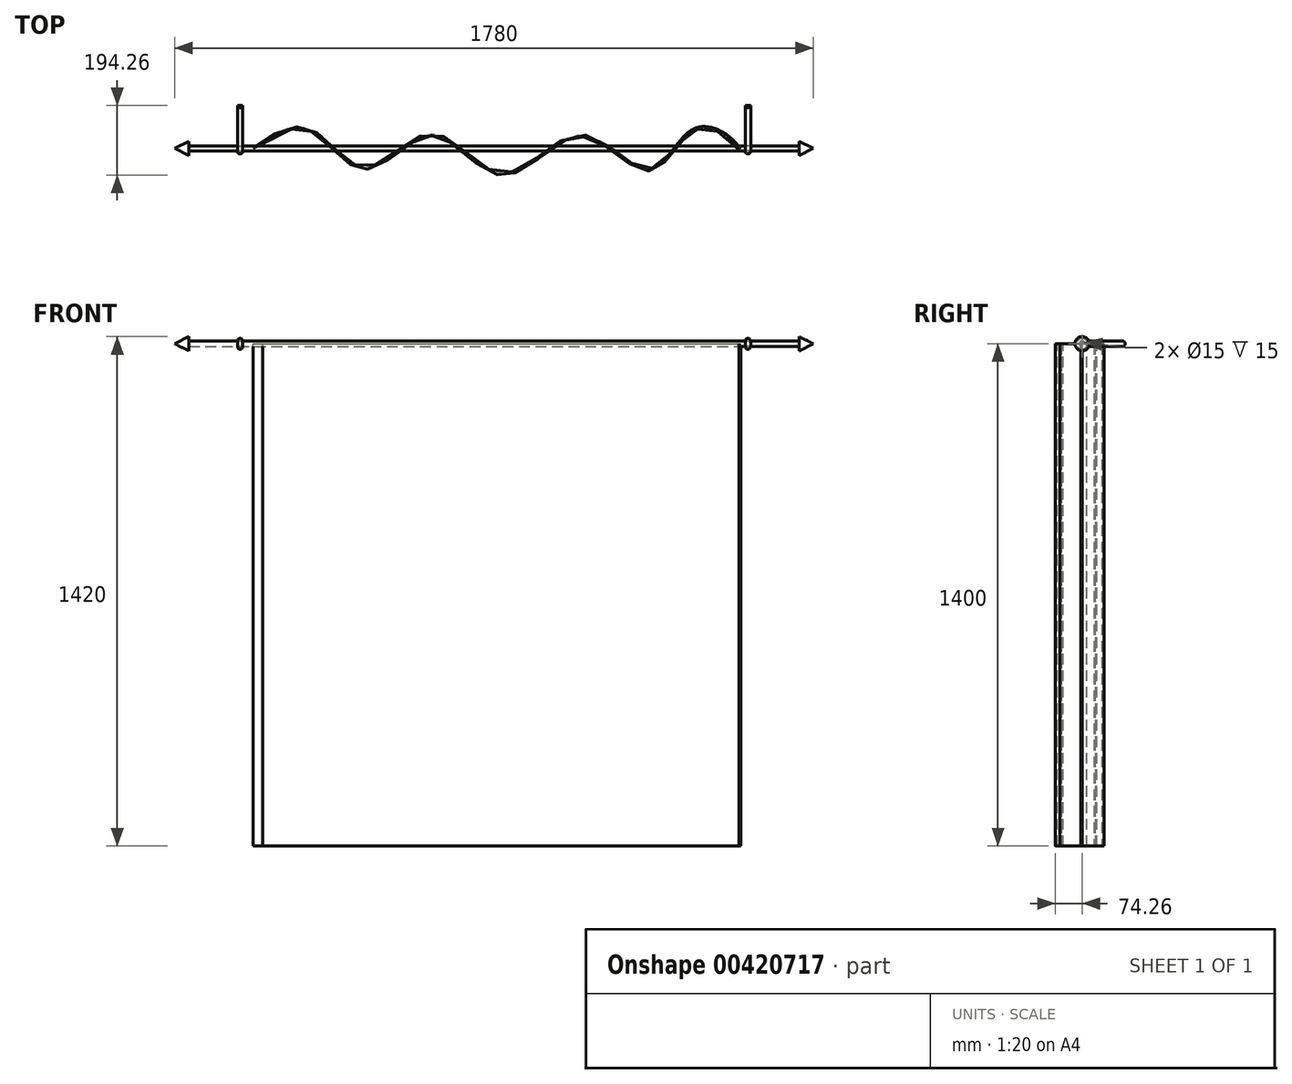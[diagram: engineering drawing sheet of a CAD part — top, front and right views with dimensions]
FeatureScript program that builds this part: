
annotation { "Feature Type Name" : "Feature", "Feature Type Description" : "" }
export const myFeature = defineFeature(function(context is Context, id is Id, definition is map)
    precondition{}
    {
        {
            var Q0;
            Q0=qCreatedBy(makeId("Front.planeOp"),FACE);
            var sketch = newSketch(context, id + "F0", { "sketchPlane" : qUnion([Q0])});
            skLineSegment(sketch, "E0", {"start": v(-890, 0) * mm, "end": v(-850, 20) * mm});
            skLineSegment(sketch, "E1", {"start": v(-850, 20) * mm, "end": v(-850, 7.5) * mm});
            skLineSegment(sketch, "E2", {"start": v(-850, 7.5) * mm, "end": v(850, 7.5) * mm});
            skLineSegment(sketch, "E3", {"start": v(850, 7.5) * mm, "end": v(850, 20) * mm});
            skLineSegment(sketch, "E4", {"start": v(850, 20) * mm, "end": v(890, 0) * mm});
            skLineSegment(sketch, "E5", {"start": v(890, 0) * mm, "end": v(-890, 0) * mm});
            skSolve(sketch);
        }
        {
            var Q0;
            Q0 = qSketchRegion(id + "F0", true);
            var Q1;
            Q1=sQuery(id+"F0.wireOp",EDGE,"E5");
            revolve(context, id + "F1", {"entities" : qUnion([Q0]), "axis" : qUnion([Q1]), "revolveType" : RevolveType.FULL});
        }
        {
            var Q0;
            Q0=qCreatedBy(makeId("Right.planeOp"),FACE);
            cPlane(context, id + "F2", {"entities" : qUnion([Q0]), "cplaneType" : CPlaneType.OFFSET, "offset" : 700 * mm, "width" : 150 * mm, "height" : 150 * mm});
        }
        {
            var Q0;
            Q0=qCreatedBy(id+"F2.planeOp",FACE);
            var sketch = newSketch(context, id + "F3", { "sketchPlane" : qUnion([Q0])});
            skLineSegment(sketch, "E6.bottom", {"start": v(13, 7.5) * mm, "end": v(120, 7.5) * mm});
            skLineSegment(sketch, "E6.top", {"start": v(13, -7.5) * mm, "end": v(120, -7.5) * mm});
            skLineSegment(sketch, "E6.right", {"start": v(120, 7.5) * mm, "end": v(120, -7.5) * mm});
            skArc(sketch, "E7", {"start": v(13, 7.5) * mm, "mid": v(-15, 0) * mm, "end": v(13, -7.5) * mm});
            skCircle(sketch, "E8", {"center": v(0, 0) * mm, "radius": 7.5 * mm});
            skSolve(sketch);
        }
        {
            var Q0;
            Q0 = qSketchRegion(id + "F3", true);
            extrude(context, id + "F4", {"entities" : qUnion([Q0]), "depth" : 15 * mm});
        }
        {
            var Q0;
            Q0=makeQuery(id+"F4.opExtrude","SWEPT_FACE",FACE,{"disambiguationData":[OSD([sQuery(id+"F3.wireOp",EDGE,"E6.bottom")])]});
            var Q1;
            Q1=makeQuery(id+"F4.opExtrude","SWEPT_FACE",FACE,{"disambiguationData":[OSD([sQuery(id+"F3.wireOp",EDGE,"E7")])]});
            var Q2;
            Q2=makeQuery(id+"F4.opExtrude","SWEPT_FACE",FACE,{"disambiguationData":[OSD([sQuery(id+"F3.wireOp",EDGE,"E6.top")])]});
            fillet(context, id + "F5", {"entities" : qUnion([Q0, Q1, Q2]), "radius" : 7 * mm, "tangentPropagation" : true, "allowEdgeOverflow" : false});
        }
        {
            var Q0;
            Q0=makeQuery(id+"F4.opExtrude","SWEPT_BODY",BODY,{"disambiguationData":[OSD([sQuery(id+"F3.wireOp",EDGE,"E6.bottom"),sQuery(id+"F3.wireOp",EDGE,"E6.top"),sQuery(id+"F3.wireOp",EDGE,"E6.right"),sQuery(id+"F3.wireOp",EDGE,"E7"),sQuery(id+"F3.wireOp",EDGE,"E8")])]});
            var Q1;
            Q1=qCreatedBy(makeId("Right.planeOp"),FACE);
            mirror(context, id + "F6", {"entities" : qUnion([Q0]), "mirrorPlane" : qUnion([Q1])});
        }
        {
            var Q0;
            Q0=qCreatedBy(makeId("Top.planeOp"),FACE);
            var sketch = newSketch(context, id + "F7", { "sketchPlane" : qUnion([Q0])});
            skFitSpline(sketch, "E9", {"points": [v(-670.7, 0) * mm, v(-511.22, 53.01) * mm, v(-357.7, -52.8) * mm, v(-171.25, 41.12) * mm, v(23.85, -69.2) * mm, v(242.94, 38.1) * mm, v(432.22, -57.28) * mm, v(558.91, 56) * mm, v(687.09, 0) * mm], "startDerivative": vector(1447.74, 1108.62) * mm, "endDerivative": vector(827.37, -1148.13) * mm});
            skFitSpline(sketch, "E10.0", {"points": [v(-667.65, -3.97) * mm, v(-660.15, 1.78) * mm, v(-645.26, 12.85) * mm, v(-623.32, 27.6) * mm, v(-601.84, 39.85) * mm, v(-580.9, 49.01) * mm, v(-563.98, 53.6) * mm, v(-550.8, 55.2) * mm, v(-541.07, 55.3) * mm, v(-531.5, 54.26) * mm, v(-523.62, 52.37) * mm, v(-517.36, 50.2) * mm, v(-512.69, 48.25) * mm, v(-508.01, 45.94) * mm, v(-501.76, 42.4) * mm, v(-493.92, 37.2) * mm, v(-484.49, 29.92) * mm, v(-475.04, 21.82) * mm, v(-462.42, 10.21) * mm, v(-446.57, -5.24) * mm, v(-430.52, -20.46) * mm, v(-417.45, -31.63) * mm, v(-407.5, -39.26) * mm, v(-397.36, -45.95) * mm, v(-386.97, -51.44) * mm, v(-378.06, -54.8) * mm, v(-370.77, -56.62) * mm, v(-365.23, -57.51) * mm, v(-360.54, -57.83) * mm, v(-356.76, -57.81) * mm, v(-352.97, -57.6) * mm, v(-348.24, -57.02) * mm, v(-340.7, -55.44) * mm, v(-331.28, -52.35) * mm, v(-320.02, -47.2) * mm, v(-308.77, -40.85) * mm, v(-297.5, -33.6) * mm, v(-286.2, -25.66) * mm, v(-271.1, -14.52) * mm, v(-252.2, -0.14) * mm, v(-233.3, 13.17) * mm, v(-218.32, 22.18) * mm, v(-207.17, 27.9) * mm, v(-196.18, 32.3) * mm, v(-187.17, 34.74) * mm, v(-180.06, 35.83) * mm, v(-175.66, 36.15) * mm, v(-172.17, 36.17) * mm, v(-168.69, 36.02) * mm, v(-164.32, 35.55) * mm, v(-159.05, 34.53) * mm, v(-151.98, 32.59) * mm, v(-143.06, 29.13) * mm, v(-132.24, 23.52) * mm, v(-117.69, 14.4) * mm, v(-99.31, 0.5) * mm, v(-77.02, -18.28) * mm, v(-58.23, -34.02) * mm, v(-43.01, -45.7) * mm, v(-31.48, -53.77) * mm, v(-19.8, -60.9) * mm, v(-7.94, -66.81) * mm, v(2.12, -70.52) * mm, v(10.3, -72.6) * mm, v(16.49, -73.7) * mm, v(21.7, -74.16) * mm, v(25.9, -74.26) * mm, v(30.08, -74.17) * mm, v(35.3, -73.73) * mm, v(43.65, -72.35) * mm, v(54.02, -69.49) * mm, v(66.4, -64.5) * mm, v(78.71, -58.23) * mm, v(91, -50.92) * mm, v(103.27, -42.81) * mm, v(119.61, -31.24) * mm, v(140.04, -15.93) * mm, v(164.5, 1.94) * mm, v(184.77, 14.85) * mm, v(200.84, 23.1) * mm, v(212.78, 28) * mm, v(222.62, 30.87) * mm, v(230.42, 32.34) * mm, v(236.23, 33) * mm, v(241.04, 33.17) * mm, v(244.88, 33.06) * mm, v(248.74, 32.8) * mm, v(253.57, 32.18) * mm, v(261.33, 30.6) * mm, v(271.11, 27.58) * mm, v(282.92, 22.51) * mm, v(294.75, 16.22) * mm, v(310.52, 6.53) * mm, v(330.08, -7.4) * mm, v(349.27, -22.07) * mm, v(364.31, -33.23) * mm, v(375.44, -41.05) * mm, v(386.4, -48.08) * mm, v(397.2, -54.06) * mm, v(407.89, -58.72) * mm, v(416.72, -61.26) * mm, v(423.77, -62.3) * mm, v(428.16, -62.5) * mm, v(431.65, -62.37) * mm, v(435.13, -62.02) * mm, v(439.39, -61.2) * mm, v(444.36, -59.68) * mm, v(450.8, -56.96) * mm, v(458.5, -52.42) * mm, v(467.3, -45.52) * mm, v(475.75, -37.45) * mm, v(483.98, -28.47) * mm, v(494.76, -15.63) * mm, v(508.02, 1.4) * mm, v(521.39, 17.97) * mm, v(532.3, 29.9) * mm, v(540.62, 37.91) * mm, v(547.67, 43.6) * mm, v(553.4, 47.43) * mm, v(557, 49.5) * mm, v(559.9, 50.96) * mm, v(562.82, 52.28) * mm, v(566.52, 53.67) * mm, v(571.05, 54.95) * mm, v(577.18, 56.17) * mm, v(585.04, 56.8) * mm, v(594.7, 56.2) * mm, v(604.51, 54.33) * mm, v(617.67, 50.27) * mm, v(634.02, 42.48) * mm, v(652.62, 29.63) * mm, v(669.4, 14.22) * mm, v(678.86, 2.86) * mm, v(683.03, -2.92) * mm]});
            skLineSegment(sketch, "E11", {"start": v(-670.7, 0) * mm, "end": v(-643.76, 13.64) * mm});
            skLineSegment(sketch, "E12", {"start": v(683.03, -2.92) * mm, "end": v(687.09, 0) * mm});
            skSolve(sketch);
        }
        {
            var Q0;
            Q0 = qSketchRegion(id + "F7", true);
            extrude(context, id + "F8", {"entities" : qUnion([Q0]), "oppositeDirection" : true, "depth" : 1400 * mm});
        }
    });
